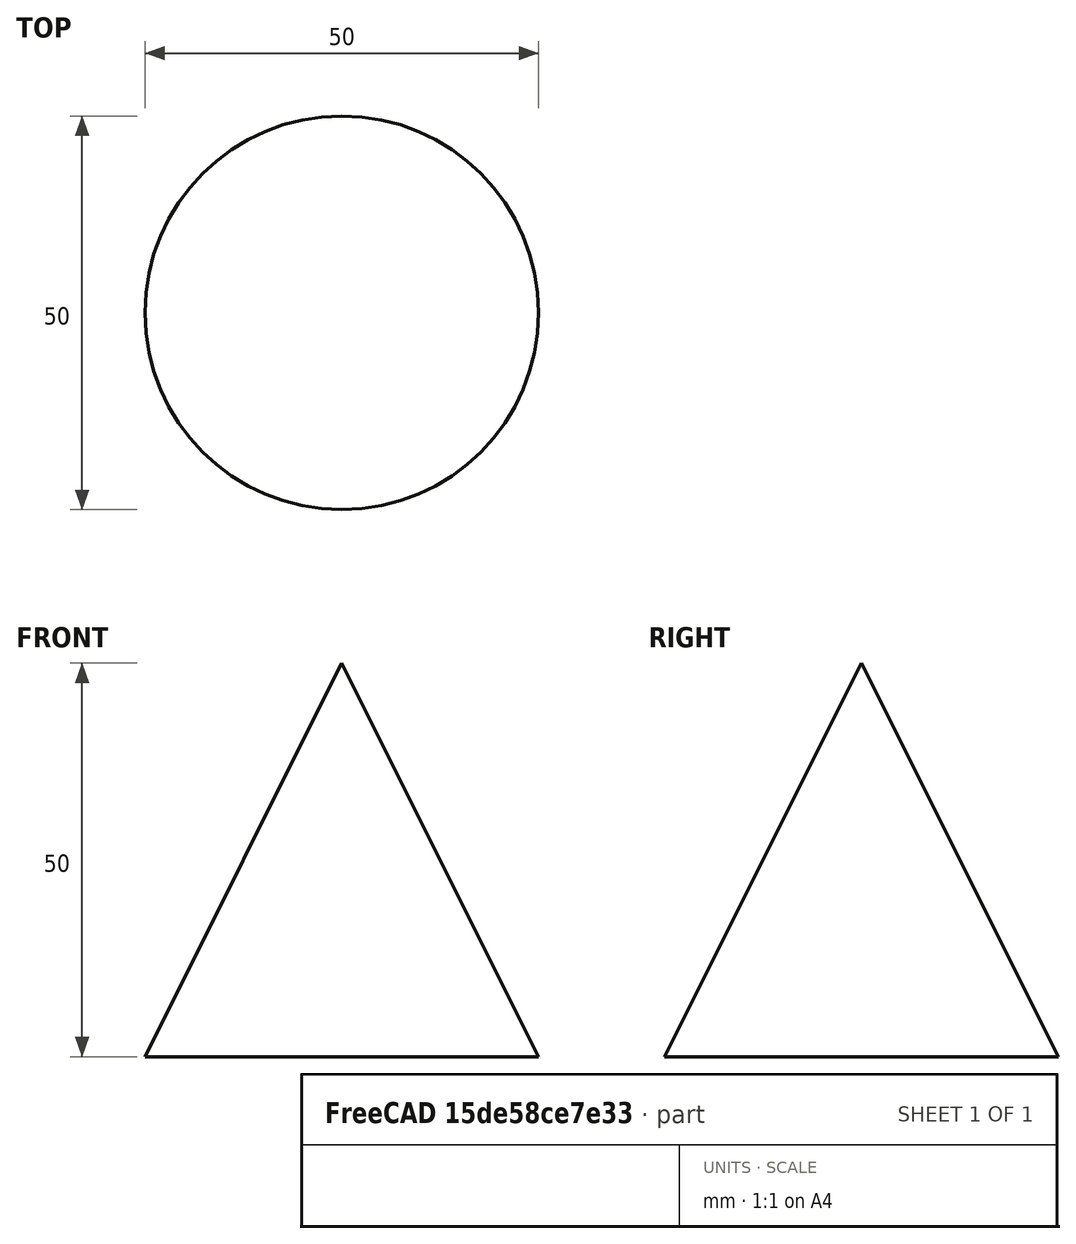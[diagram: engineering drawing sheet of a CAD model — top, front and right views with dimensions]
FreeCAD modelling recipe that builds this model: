
FCSTD DOCUMENT  (FreeCAD 0.18.4R)
Label: drill
License: All rights reserved
LicenseURL: http://en.wikipedia.org/wiki/All_rights_reserved
objects: Sketcher::SketchObject×1, PartDesign::Revolution×1, PartDesign::Body×1
note: 4 computed .brp shape members not serialized (recipe doc carries the construction recipe); baked Part::Feature solids carry a one-line shape summary decoded from their .brp

FEATURE [Sketcher::SketchObject] Sketch
  MapMode = 5
  Placement = pos=(0,0,0) rot=(1,0,0;1.5708rad)
  Support = -> [XZ_Plane]
  sketch-geometry (3):
    g0: LineSegment StartX=0 StartY=50 StartZ=0 EndX=-25 EndY=0 EndZ=0
    g1: LineSegment StartX=-25 StartY=0 StartZ=0 EndX=0 EndY=0 EndZ=0
    g2: LineSegment StartX=0 StartY=0 StartZ=0 EndX=0 EndY=50 EndZ=0
  constraints (9):
    c: Coincident(g0,g1)
    c: Coincident(g1,g2)
    c: Coincident(g2,g0)
    c: DistanceY(g1,g0) = 50
    c: DistanceY(g1,g0) = 0
    c: DistanceX(g0,g1) = 25
    c: DistanceX(g0,g1) = 0
    c: DistanceX(g1,g-1) = 0
    c: DistanceY(g1,g-1) = 0
FEATURE [PartDesign::Revolution] Revolution
  Angle = 360
  Axis = (0,2e-16,1)
  Base = (0,0,0)
  Midplane = true
  Placement = pos=(0,0,0) rot=(1,0,0;1.5708rad)
  Profile = -> Sketch
  ReferenceAxis = -> Sketch [V_Axis]
FEATURE [PartDesign::Body] Body
  Group = -> [Sketch,Revolution]
  Origin = -> Origin
  Tip = -> Revolution
